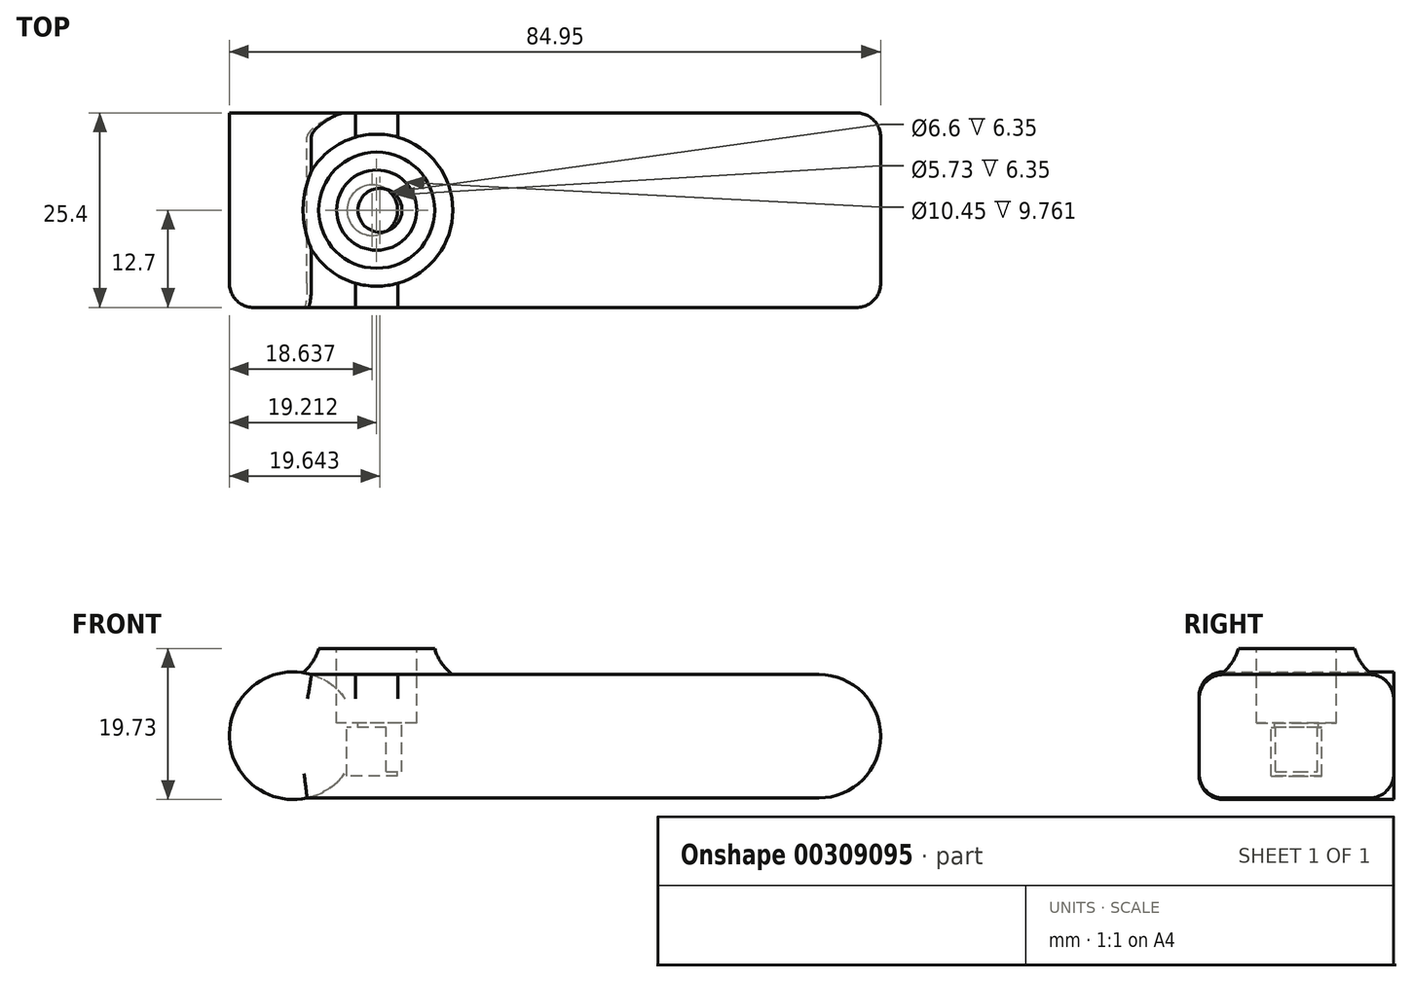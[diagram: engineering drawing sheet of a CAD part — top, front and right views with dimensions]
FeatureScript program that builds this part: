
annotation { "Feature Type Name" : "Feature", "Feature Type Description" : "" }
export const myFeature = defineFeature(function(context is Context, id is Id, definition is map)
    precondition{}
    {
        {
            var Q0;
            Q0=qCreatedBy(makeId("Front.planeOp"),FACE);
            var sketch = newSketch(context, id + "F0", { "sketchPlane" : qUnion([Q0])});
            skArc(sketch, "E0", {"start": v(-39.14, 6.9) * mm, "mid": v(-49.84, -0.78) * mm, "end": v(-39.72, -9.2) * mm});
            skLineSegment(sketch, "E1", {"start": v(-39.14, 6.9) * mm, "end": v(27.05, 6.9) * mm});
            skLineSegment(sketch, "E2", {"start": v(-39.72, -9.2) * mm, "end": v(27.05, -9.2) * mm});
            skArc(sketch, "E3", {"start": v(27.05, -9.2) * mm, "mid": v(35.11, -1.15) * mm, "end": v(27.05, 6.9) * mm});
            skSolve(sketch);
        }
        {
            var Q0;
            Q0 = qSketchRegion(id + "F0", true);
            extrude(context, id + "F1", {"entities" : qUnion([Q0]), "endBound" : BoundingType.SYMMETRIC, "depth" : 25.4 * mm});
        }
        {
            var Q0;
            Q0=qCreatedBy(makeId("Front.planeOp"),FACE);
            var sketch = newSketch(context, id + "F2", { "sketchPlane" : qUnion([Q0])});
            skLineSegment(sketch, "E4", {"start": v(-30.63, 0) * mm, "end": v(-30.63, 58.04) * mm});
            skLineSegment(sketch, "E5", {"start": v(-30.63, 58.04) * mm, "end": v(-30.63, -56.93) * mm});
            skSolve(sketch);
        }
        {
            var Q0;
            Q0=qCreatedBy(makeId("Front.planeOp"),FACE);
            var sketch = newSketch(context, id + "F3", { "sketchPlane" : qUnion([Q0])});
            skArc(sketch, "E6", {"start": v(-23.05, 10.32) * mm, "mid": v(-21.59, 7.68) * mm, "end": v(-19.05, 6.06) * mm});
            skLineSegment(sketch, "E7", {"start": v(-23.05, 10.32) * mm, "end": v(-25.4, 10.32) * mm});
            skLineSegment(sketch, "E8", {"start": v(-25.4, 10.32) * mm, "end": v(-25.4, 6.06) * mm});
            skLineSegment(sketch, "E9", {"start": v(-25.4, 6.06) * mm, "end": v(-19.05, 6.06) * mm});
            skSolve(sketch);
        }
        {
            var Q0;
            Q0=makeQuery(id+"F3.imprint","IMPRINT",FACE,{"disambiguationData":[TD([[makeQuery(id+"F3.imprint","IMPRINT",EDGE,{"derivedFrom":sQuery(id+"F3.wireOp",EDGE,"E6")}),-1.0]])]});
            var Q1;
            Q1=sQuery(id+"F2.wireOp",EDGE,"E5");
            revolve(context, id + "F4", {"operationType" : NewBodyOperationType.ADD, "entities" : qUnion([Q0]), "axis" : qUnion([Q1]), "revolveType" : RevolveType.FULL});
        }
        {
            var Q0;
            Q0=qCreatedBy(makeId("Top.planeOp"),FACE);
            var sketch = newSketch(context, id + "F5", { "sketchPlane" : qUnion([Q0])});
            skCircle(sketch, "E10", {"center": v(-31.2, 0) * mm, "radius": 3.3 * mm});
            skSolve(sketch);
        }
        {
            var Q0;
            Q0 = qSketchRegion(id + "F5", true);
            var Q1;
            Q1=makeQuery(id+"F4.boolean.opBoolean","SPLIT",FACE,{"disambiguationData":[TD([makeQuery(id+"F4.opRevolve","SWEPT_FACE",FACE,{"disambiguationData":[OSD([sQuery(id+"F3.wireOp",EDGE,"E8")])]})])],"derivedFrom":makeQuery(id+"F1.opExtrude","SWEPT_FACE",FACE,{"disambiguationData":[OSD([sQuery(id+"F0.wireOp",EDGE,"E1")])]})});
            extrude(context, id + "F6", {"entities" : qUnion([Q0, Q1]), "operationType" : NewBodyOperationType.REMOVE, "oppositeDirection" : true, "depth" : 6.35 * mm});
        }
        {
            var Q0;
            Q0 = qSketchRegion(id + "F5", true);
            extrude(context, id + "F7", {"entities" : qUnion([Q0]), "operationType" : NewBodyOperationType.REMOVE, "oppositeDirection" : true, "depth" : 6.35 * mm});
        }
        {
            var Q0;
            Q0 = qSketchRegion(id + "F5", true);
            extrude(context, id + "F8", {"entities" : qUnion([Q0]), "operationType" : NewBodyOperationType.REMOVE, "oppositeDirection" : true, "depth" : 6.35 * mm});
        }
        {
            var Q0;
            Q0=makeQuery(id+"F6.boolean.opBoolean","COPY",FACE,{"derivedFrom":makeQuery(id+"F6.opExtrude","CAP_FACE",FACE,{"disambiguationData":[OSD([sQuery(id+"F0.wireOp",EDGE,"E1")])],"isStart":false})});
            var sketch = newSketch(context, id + "F9", { "sketchPlane" : qUnion([Q0])});
            skCircle(sketch, "E11", {"center": v(-30.2, 0) * mm, "radius": 2.87 * mm});
            skSolve(sketch);
        }
        {
            var Q0;
            Q0 = qSketchRegion(id + "F9", true);
            extrude(context, id + "F10", {"entities" : qUnion([Q0]), "operationType" : NewBodyOperationType.REMOVE, "oppositeDirection" : true, "depth" : 6.35 * mm});
        }
        {
            var Q0;
            Q0=makeQuery(id+"F1.opExtrude","CAP_EDGE",EDGE,{"disambiguationData":[OSD([sQuery(id+"F0.wireOp",EDGE,"E1")])],"isStart":false});
            var Q1;
            Q1=makeQuery(id+"F1.opExtrude","CAP_EDGE",EDGE,{"disambiguationData":[OSD([sQuery(id+"F0.wireOp",EDGE,"E1")])],"isStart":true});
            var Q2;
            Q2=makeQuery(id+"F1.opExtrude","CAP_EDGE",EDGE,{"disambiguationData":[OSD([sQuery(id+"F0.wireOp",EDGE,"E0")])],"isStart":false});
            fillet(context, id + "F11", {"entities" : qUnion([Q0, Q1, Q2]), "radius" : 3.17 * mm, "tangentPropagation" : true, "allowEdgeOverflow" : false});
        }
    });
